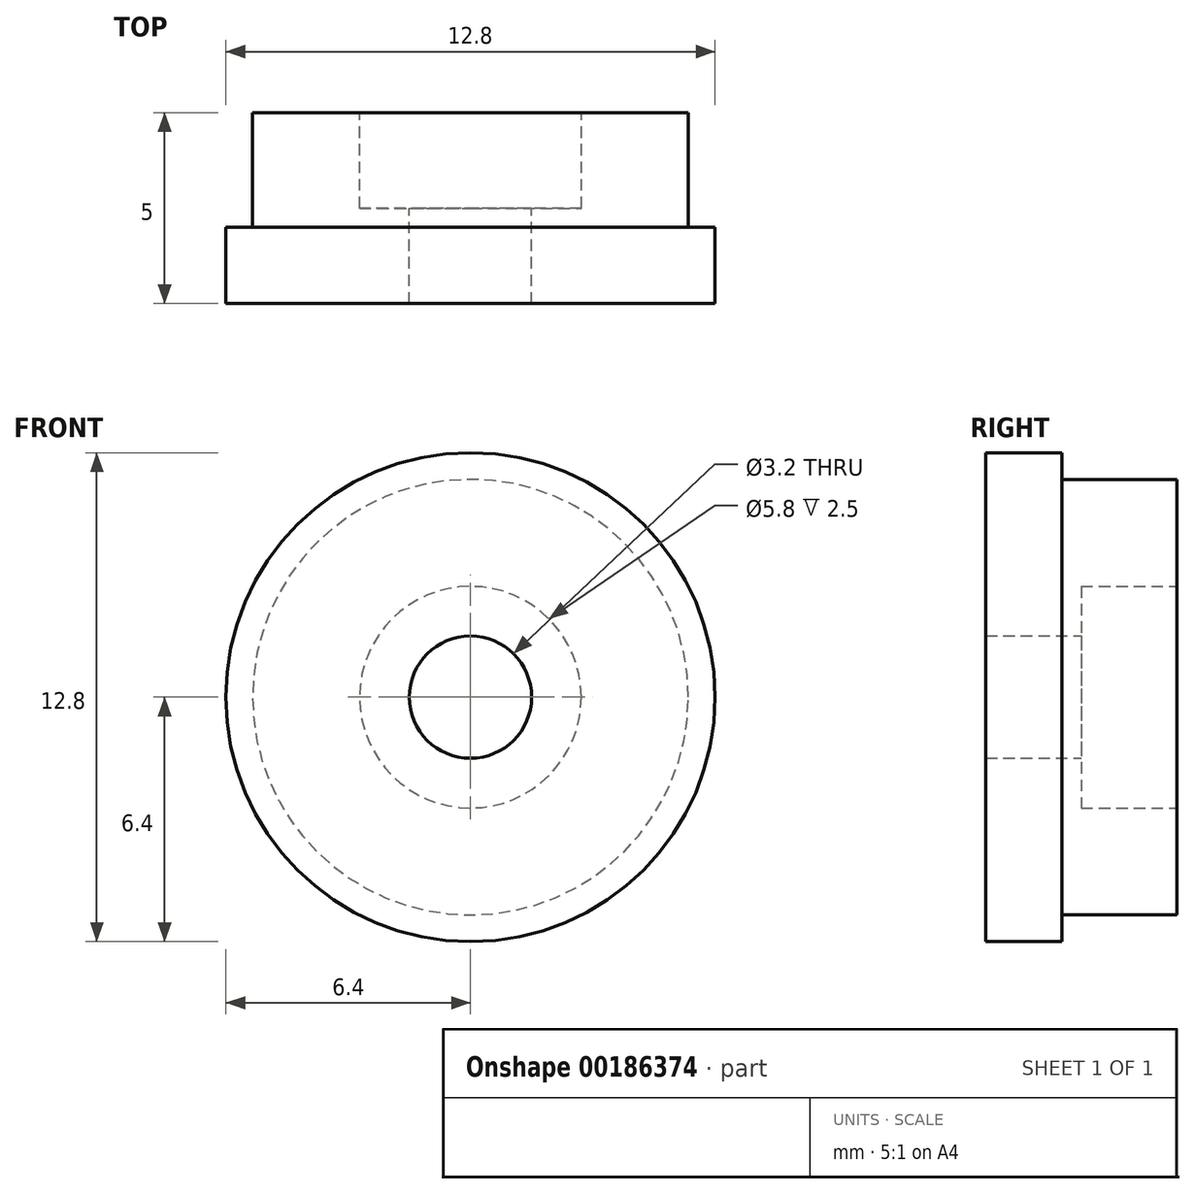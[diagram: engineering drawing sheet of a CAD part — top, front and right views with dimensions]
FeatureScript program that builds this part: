
annotation { "Feature Type Name" : "Feature", "Feature Type Description" : "" }
export const myFeature = defineFeature(function(context is Context, id is Id, definition is map)
    precondition{}
    {
        {
            var Q0;
            Q0=qCreatedBy(makeId("Right.planeOp"),FACE);
            var sketch = newSketch(context, id + "F0", { "sketchPlane" : qUnion([Q0])});
            skLineSegment(sketch, "E0", {"start": v(11.47, 0) * mm, "end": v(0, 0) * mm, "construction": true});
            skLineSegment(sketch, "E1", {"start": v(2.5, 1.6) * mm, "end": v(0, 1.6) * mm});
            skLineSegment(sketch, "E2", {"start": v(2.5, 1.6) * mm, "end": v(2.5, 2.9) * mm});
            skLineSegment(sketch, "E3", {"start": v(5, 2.9) * mm, "end": v(2.5, 2.9) * mm});
            skLineSegment(sketch, "E4", {"start": v(5, 2.9) * mm, "end": v(5, 5.7) * mm});
            skLineSegment(sketch, "E5", {"start": v(2, 5.7) * mm, "end": v(5, 5.7) * mm});
            skLineSegment(sketch, "E6", {"start": v(2, 5.7) * mm, "end": v(2, 6.4) * mm});
            skLineSegment(sketch, "E7", {"start": v(0, 6.4) * mm, "end": v(2, 6.4) * mm});
            skLineSegment(sketch, "E8", {"start": v(0, 6.4) * mm, "end": v(0, 1.6) * mm});
            skSolve(sketch);
        }
        {
            var Q0;
            Q0=makeQuery(id+"F0.imprint","IMPRINT",FACE,{"disambiguationData":[TD([[makeQuery(id+"F0.imprint","IMPRINT",EDGE,{"derivedFrom":sQuery(id+"F0.wireOp",EDGE,"E1")}),-1.0]])]});
            var Q1;
            Q1=sQuery(id+"F0.wireOp",EDGE,"E0");
            revolve(context, id + "F1", {"entities" : qUnion([Q0]), "axis" : qUnion([Q1]), "revolveType" : RevolveType.FULL});
        }
    });
